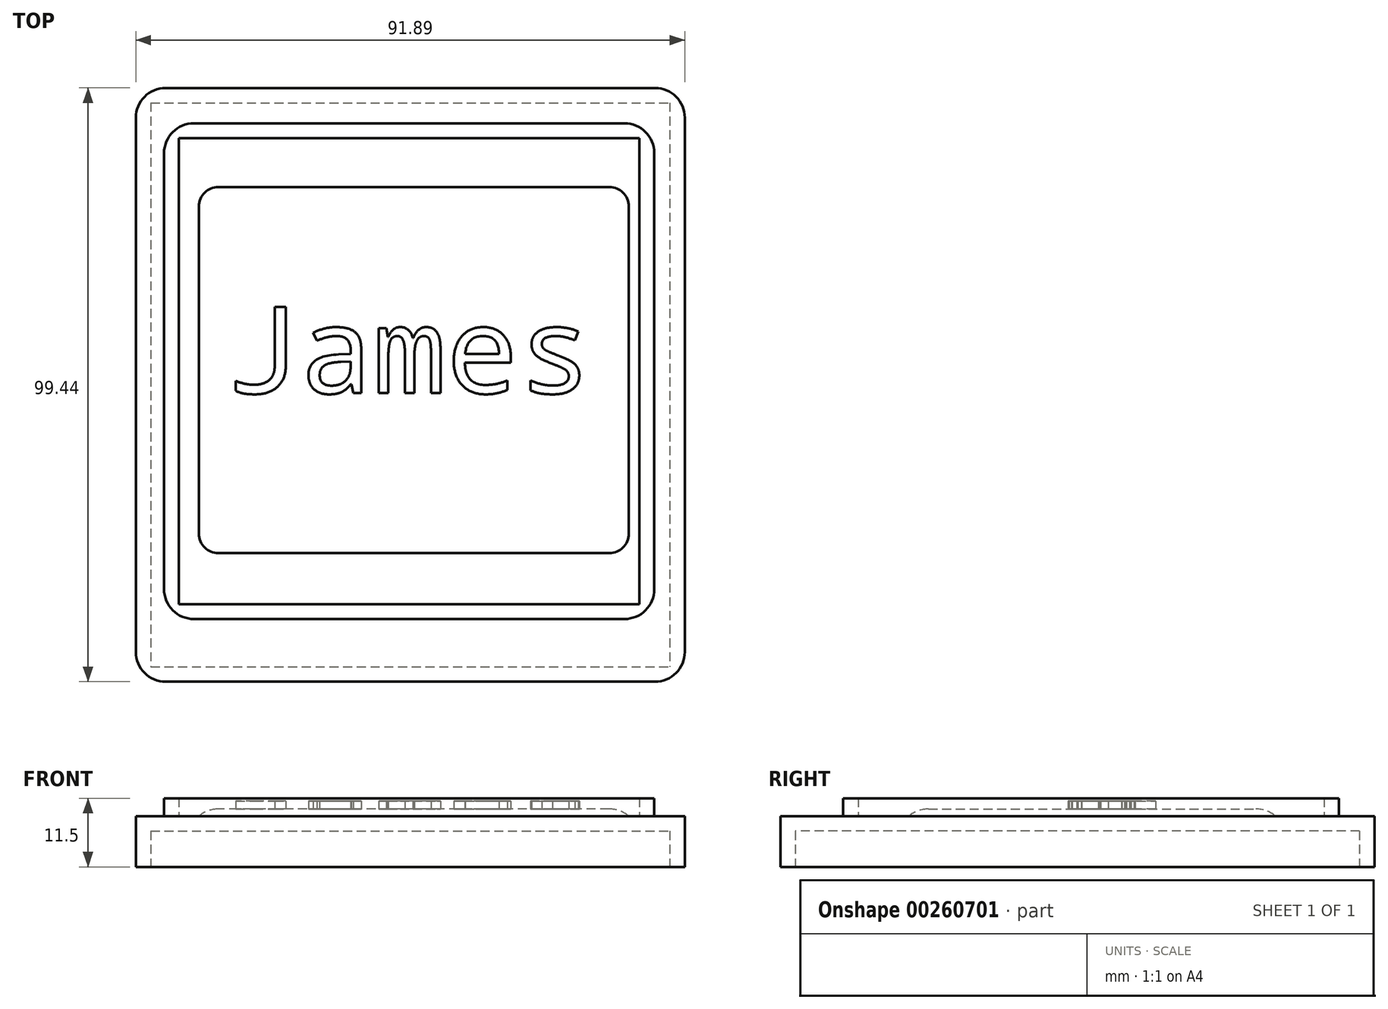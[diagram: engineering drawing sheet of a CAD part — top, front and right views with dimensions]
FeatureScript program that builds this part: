
annotation { "Feature Type Name" : "Feature", "Feature Type Description" : "" }
export const myFeature = defineFeature(function(context is Context, id is Id, definition is map)
    precondition{}
    {
        {
            var Q0;
            Q0=qCreatedBy(makeId("Top.planeOp"),FACE);
            var sketch = newSketch(context, id + "F0", { "sketchPlane" : qUnion([Q0])});
            skLineSegment(sketch, "E0.bottom", {"start": v(-46.57, 62.32) * mm, "end": v(45.32, 62.32) * mm});
            skLineSegment(sketch, "E0.top", {"start": v(-46.57, -37.12) * mm, "end": v(45.32, -37.12) * mm});
            skLineSegment(sketch, "E0.left", {"start": v(-46.57, 62.32) * mm, "end": v(-46.57, -37.12) * mm});
            skLineSegment(sketch, "E0.right", {"start": v(45.32, 62.32) * mm, "end": v(45.32, -37.12) * mm});
            skSolve(sketch);
        }
        {
            var Q0;
            Q0=makeQuery(id+"F0.imprint","IMPRINT",FACE,{"disambiguationData":[TD([[makeQuery(id+"F0.imprint","IMPRINT",EDGE,{"derivedFrom":sQuery(id+"F0.wireOp",EDGE,"E0.bottom")}),-1.0]])]});
            extrude(context, id + "F1", {"entities" : qUnion([Q0]), "depth" : 8.5 * mm});
        }
        {
            var Q0;
            Q0=makeQuery(id+"F1.opExtrude","CAP_FACE",FACE,{"disambiguationData":[OSD([sQuery(id+"F0.wireOp",EDGE,"E0.bottom"),sQuery(id+"F0.wireOp",EDGE,"E0.top"),sQuery(id+"F0.wireOp",EDGE,"E0.left"),sQuery(id+"F0.wireOp",EDGE,"E0.right")])],"isStart":true});
            shell(context, id + "F2", {"entities" : qUnion([Q0]), "thickness" : 2.5 * mm});
        }
        {
            var Q0;
            Q0=makeQuery(id+"F1.opExtrude","CAP_FACE",FACE,{"disambiguationData":[OSD([sQuery(id+"F0.wireOp",EDGE,"E0.bottom"),sQuery(id+"F0.wireOp",EDGE,"E0.top"),sQuery(id+"F0.wireOp",EDGE,"E0.left"),sQuery(id+"F0.wireOp",EDGE,"E0.right")])],"isStart":false});
            var sketch = newSketch(context, id + "F3", { "sketchPlane" : qUnion([Q0])});
            skLineSegment(sketch, "E1.bottom", {"start": v(-41.85, 56.4) * mm, "end": v(40.2, 56.4) * mm});
            skLineSegment(sketch, "E1.top", {"start": v(-41.85, -26.62) * mm, "end": v(40.2, -26.62) * mm});
            skLineSegment(sketch, "E1.left", {"start": v(-41.85, 56.4) * mm, "end": v(-41.85, -26.62) * mm});
            skLineSegment(sketch, "E1.right", {"start": v(40.2, 56.4) * mm, "end": v(40.2, -26.62) * mm});
            skSolve(sketch);
        }
        {
            var Q0;
            Q0=makeQuery(id+"F3.imprint","IMPRINT",FACE,{"disambiguationData":[TD([[makeQuery(id+"F3.imprint","IMPRINT",EDGE,{"derivedFrom":sQuery(id+"F3.wireOp",EDGE,"E1.bottom")}),-1.0]])]});
            extrude(context, id + "F4", {"entities" : qUnion([Q0]), "operationType" : NewBodyOperationType.ADD, "depth" : 3 * mm});
        }
        {
            var Q0;
            Q0=makeQuery(id+"F4.opExtrude","CAP_FACE",FACE,{"disambiguationData":[OSD([sQuery(id+"F3.wireOp",EDGE,"E1.bottom"),sQuery(id+"F3.wireOp",EDGE,"E1.top"),sQuery(id+"F3.wireOp",EDGE,"E1.left"),sQuery(id+"F3.wireOp",EDGE,"E1.right")])],"isStart":false});
            shell(context, id + "F5", {"entities" : qUnion([Q0]), "thickness" : 2.5 * mm});
        }
        {
            var Q0;
            Q0=makeQuery(id+"F1.opExtrude","SWEPT_EDGE",EDGE,{"disambiguationData":[OSD([sQuery(id+"F0.wireOp",EDGE,"E0.top"),sQuery(id+"F0.wireOp",EDGE,"E0.left")])]});
            var Q1;
            Q1=makeQuery(id+"F4.opExtrude","SWEPT_EDGE",EDGE,{"disambiguationData":[OSD([sQuery(id+"F3.wireOp",EDGE,"E1.top"),sQuery(id+"F3.wireOp",EDGE,"E1.left")])]});
            var Q2;
            Q2=makeQuery(id+"F1.opExtrude","SWEPT_EDGE",EDGE,{"disambiguationData":[OSD([sQuery(id+"F0.wireOp",EDGE,"E0.top"),sQuery(id+"F0.wireOp",EDGE,"E0.right")])]});
            var Q3;
            Q3=makeQuery(id+"F4.opExtrude","SWEPT_EDGE",EDGE,{"disambiguationData":[OSD([sQuery(id+"F3.wireOp",EDGE,"E1.top"),sQuery(id+"F3.wireOp",EDGE,"E1.right")])]});
            var Q4;
            Q4=makeQuery(id+"FTkW4tdqKPrA7Je_1.opExtrude","SWEPT_EDGE",EDGE,{"disambiguationData":[OSD([sQuery(id+"Fssd0YiAjEaduH3_1.wireOp",EDGE,"an16Rhwf-g9Rc-cAiP-1MTG-7YVOEeKWwYrD.bottom"),sQuery(id+"Fssd0YiAjEaduH3_1.wireOp",EDGE,"an16Rhwf-g9Rc-cAiP-1MTG-7YVOEeKWwYrD.left")])]});
            var Q5;
            Q5=makeQuery(id+"FTkW4tdqKPrA7Je_1.opExtrude","SWEPT_EDGE",EDGE,{"disambiguationData":[OSD([sQuery(id+"Fssd0YiAjEaduH3_1.wireOp",EDGE,"an16Rhwf-g9Rc-cAiP-1MTG-7YVOEeKWwYrD.bottom"),sQuery(id+"Fssd0YiAjEaduH3_1.wireOp",EDGE,"an16Rhwf-g9Rc-cAiP-1MTG-7YVOEeKWwYrD.right")])]});
            var Q6;
            Q6=makeQuery(id+"F1.opExtrude","SWEPT_EDGE",EDGE,{"disambiguationData":[OSD([sQuery(id+"F0.wireOp",EDGE,"E0.bottom"),sQuery(id+"F0.wireOp",EDGE,"E0.left")])]});
            var Q7;
            Q7=makeQuery(id+"F1.opExtrude","SWEPT_EDGE",EDGE,{"disambiguationData":[OSD([sQuery(id+"F0.wireOp",EDGE,"E0.bottom"),sQuery(id+"F0.wireOp",EDGE,"E0.right")])]});
            var Q8;
            Q8=makeQuery(id+"F4.opExtrude","SWEPT_EDGE",EDGE,{"disambiguationData":[OSD([sQuery(id+"F3.wireOp",EDGE,"E1.bottom"),sQuery(id+"F3.wireOp",EDGE,"E1.right")])]});
            var Q9;
            Q9=makeQuery(id+"F4.opExtrude","SWEPT_EDGE",EDGE,{"disambiguationData":[OSD([sQuery(id+"F3.wireOp",EDGE,"E1.bottom"),sQuery(id+"F3.wireOp",EDGE,"E1.left")])]});
            fillet(context, id + "F6", {"entities" : qUnion([Q0, Q1, Q2, Q3, Q4, Q5, Q6, Q7, Q8, Q9]), "radius" : 5 * mm, "tangentPropagation" : true, "allowEdgeOverflow" : false});
        }
        {
            var Q0;
            Q0=makeQuery(id+"F5.opShell","OFFSET_FACE",FACE,{"disambiguationData":[OSD([sQuery(id+"F0.wireOp",EDGE,"E0.bottom"),sQuery(id+"F0.wireOp",EDGE,"E0.top"),sQuery(id+"F0.wireOp",EDGE,"E0.left"),sQuery(id+"F0.wireOp",EDGE,"E0.right")])]});
            var sketch = newSketch(context, id + "F7", { "sketchPlane" : qUnion([Q0])});
            skLineSegment(sketch, "E2.bottom", {"start": v(-36, 45.73) * mm, "end": v(35.93, 45.73) * mm});
            skLineSegment(sketch, "E2.top", {"start": v(-36, -15.6) * mm, "end": v(35.93, -15.6) * mm});
            skLineSegment(sketch, "E2.left", {"start": v(-36, 45.73) * mm, "end": v(-36, -15.6) * mm});
            skLineSegment(sketch, "E2.right", {"start": v(35.93, 45.73) * mm, "end": v(35.93, -15.6) * mm});
            skSolve(sketch);
        }
        {
            var Q0;
            Q0=makeQuery(id+"F7.imprint","IMPRINT",FACE,{"disambiguationData":[TD([[makeQuery(id+"F7.imprint","IMPRINT",EDGE,{"derivedFrom":sQuery(id+"F7.wireOp",EDGE,"E2.bottom")}),-1.0]])]});
            extrude(context, id + "F8", {"entities" : qUnion([Q0]), "operationType" : NewBodyOperationType.ADD, "depth" : 1.2 * mm});
        }
        {
            var Q0;
            Q0=makeQuery(id+"F8.opExtrude","CAP_EDGE",EDGE,{"disambiguationData":[OSD([sQuery(id+"F7.wireOp",EDGE,"E2.top")])],"isStart":false});
            var Q1;
            Q1=makeQuery(id+"F8.opExtrude","CAP_EDGE",EDGE,{"disambiguationData":[OSD([sQuery(id+"F7.wireOp",EDGE,"E2.left")])],"isStart":false});
            var Q2;
            Q2=makeQuery(id+"F8.opExtrude","CAP_FACE",FACE,{"disambiguationData":[OSD([sQuery(id+"F7.wireOp",EDGE,"E2.bottom"),sQuery(id+"F7.wireOp",EDGE,"E2.top"),sQuery(id+"F7.wireOp",EDGE,"E2.left"),sQuery(id+"F7.wireOp",EDGE,"E2.right")])],"isStart":false});
            var Q3;
            Q3=makeQuery(id+"F8.opExtrude","CAP_EDGE",EDGE,{"disambiguationData":[OSD([sQuery(id+"F7.wireOp",EDGE,"E2.bottom")])],"isStart":false});
            fillet(context, id + "F9", {"entities" : qUnion([Q0, Q1, Q2, Q3]), "radius" : 5 * mm, "tangentPropagation" : true, "allowEdgeOverflow" : false});
        }
        {
            var Q0;
            Q0=makeQuery(id+"F9.opFillet","BLEND_EDGE",EDGE,{"blendedFrom":[makeQuery(id+"F8.opExtrude","CAP_EDGE",EDGE,{"disambiguationData":[OSD([sQuery(id+"F7.wireOp",EDGE,"E2.bottom")])],"isStart":false}),makeQuery(id+"F8.opExtrude","CAP_EDGE",EDGE,{"disambiguationData":[OSD([sQuery(id+"F7.wireOp",EDGE,"E2.left")])],"isStart":false})],"blendedInto":[]});
            var Q1;
            Q1=makeQuery(id+"F9.opFillet","BLEND_EDGE",EDGE,{"blendedFrom":[makeQuery(id+"F8.opExtrude","CAP_EDGE",EDGE,{"disambiguationData":[OSD([sQuery(id+"F7.wireOp",EDGE,"E2.top")])],"isStart":false}),makeQuery(id+"F8.opExtrude","CAP_EDGE",EDGE,{"disambiguationData":[OSD([sQuery(id+"F7.wireOp",EDGE,"E2.left")])],"isStart":false})],"blendedInto":[]});
            var Q2;
            Q2=makeQuery(id+"F9.opFillet","BLEND_EDGE",EDGE,{"blendedFrom":[makeQuery(id+"F8.opExtrude","CAP_EDGE",EDGE,{"disambiguationData":[OSD([sQuery(id+"F7.wireOp",EDGE,"E2.top")])],"isStart":false}),makeQuery(id+"F8.opExtrude","CAP_EDGE",EDGE,{"disambiguationData":[OSD([sQuery(id+"F7.wireOp",EDGE,"E2.right")])],"isStart":false})],"blendedInto":[]});
            var Q3;
            Q3=makeQuery(id+"F9.opFillet","BLEND_EDGE",EDGE,{"blendedFrom":[makeQuery(id+"F8.opExtrude","CAP_EDGE",EDGE,{"disambiguationData":[OSD([sQuery(id+"F7.wireOp",EDGE,"E2.bottom")])],"isStart":false}),makeQuery(id+"F8.opExtrude","CAP_EDGE",EDGE,{"disambiguationData":[OSD([sQuery(id+"F7.wireOp",EDGE,"E2.right")])],"isStart":false})],"blendedInto":[]});
            fillet(context, id + "F10", {"entities" : qUnion([Q0, Q1, Q2, Q3]), "radius" : 5 * mm, "tangentPropagation" : true, "allowEdgeOverflow" : false});
        }
        {
            var Q0;
            Q0=makeQuery(id+"F8.opExtrude","CAP_FACE",FACE,{"disambiguationData":[OSD([sQuery(id+"F7.wireOp",EDGE,"E2.bottom"),sQuery(id+"F7.wireOp",EDGE,"E2.top"),sQuery(id+"F7.wireOp",EDGE,"E2.left"),sQuery(id+"F7.wireOp",EDGE,"E2.right")])],"isStart":false});
            var sketch = newSketch(context, id + "F11", { "sketchPlane" : qUnion([Q0])});
            skText(sketch, "E3", { "text": "James", "fontName": "DroidSansMono.ttf"});
            const initialGuessF11  = {"E3": [-0.03118, 0.0112, 1, 0, 0.0146]};
            skSetInitialGuess(sketch, initialGuessF11);
            skSolve(sketch);
        }
        {
            var Q0;
            Q0 = qSketchRegion(id + "F11", true);
            extrude(context, id + "F12", {"entities" : qUnion([Q0]), "operationType" : NewBodyOperationType.ADD, "depth" : 1.3 * mm});
        }
    });
